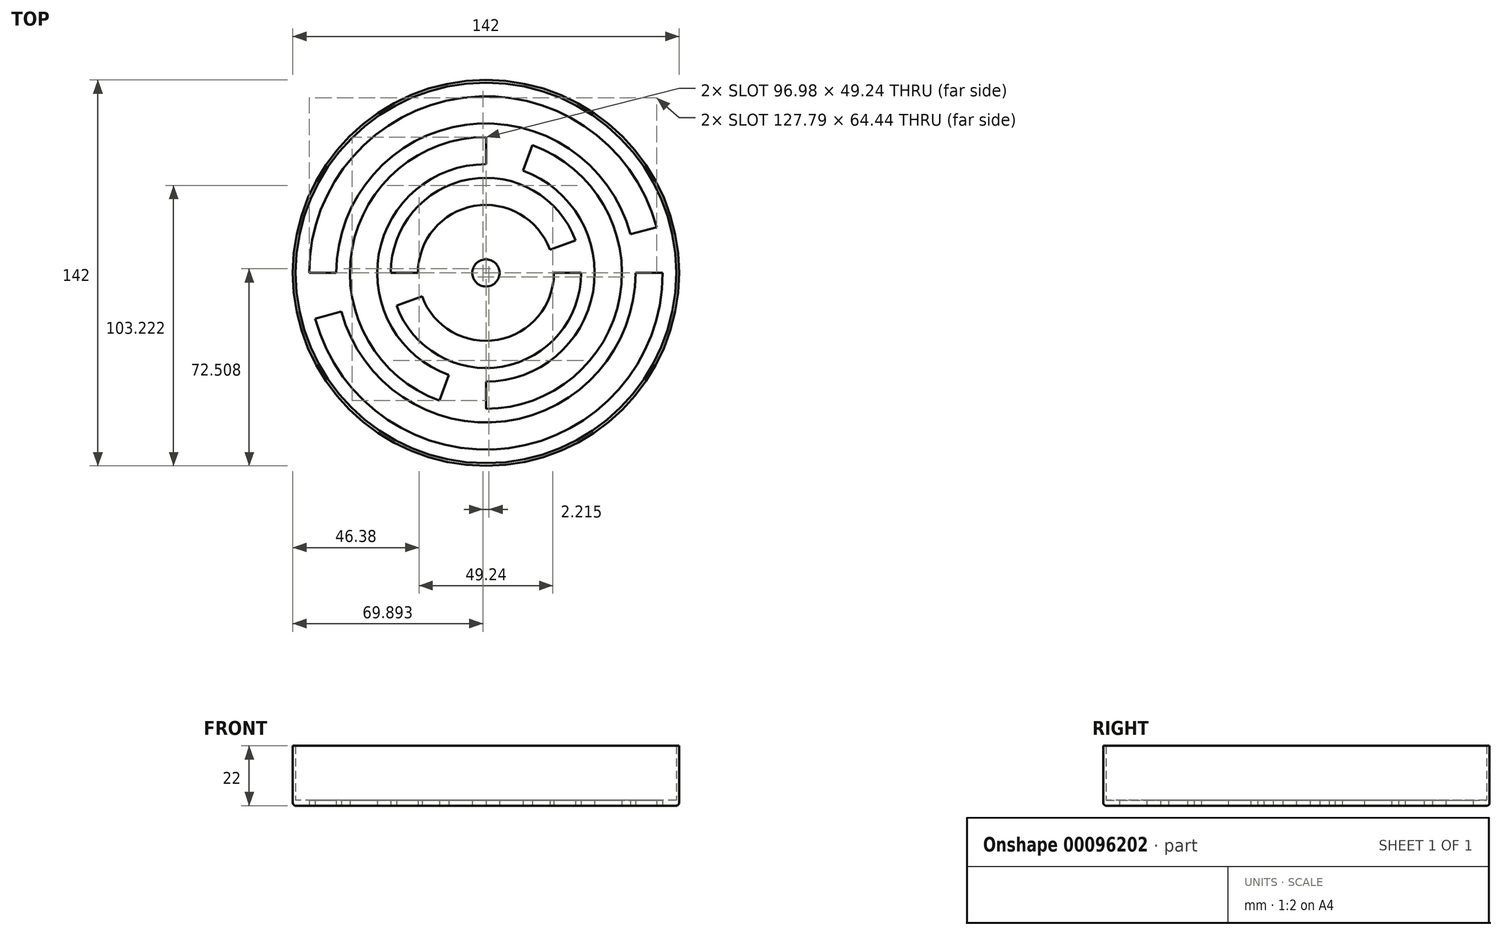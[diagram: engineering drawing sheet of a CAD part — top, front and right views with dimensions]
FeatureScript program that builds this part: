
annotation { "Feature Type Name" : "Feature", "Feature Type Description" : "" }
export const myFeature = defineFeature(function(context is Context, id is Id, definition is map)
    precondition{}
    {
        {
            assignVariable(context, id + "F0", {"name" : "wallthickness", "anyValue" : 2});
        }
        {
            assignVariable(context, id + "F1", {"name" : "height", "anyValue" : 20});
        }
        {
            var Q0;
            Q0=qCreatedBy(makeId("Top.planeOp"),FACE);
            var sketch = newSketch(context, id + "F2", { "sketchPlane" : qUnion([Q0])});
            skCircle(sketch, "E0", {"center": v(0, 0) * mm, "radius": 70 * mm});
            skCircle(sketch, "E1", {"center": v(0, 0) * mm, "radius": 71 * mm});
            skCircle(sketch, "E2", {"center": v(0, 0) * mm, "radius": 65 * mm});
            skCircle(sketch, "E3", {"center": v(0, 0) * mm, "radius": 55 * mm});
            skCircle(sketch, "E4", {"center": v(0, 0) * mm, "radius": 50 * mm});
            skCircle(sketch, "E5", {"center": v(0, 0) * mm, "radius": 40 * mm});
            skCircle(sketch, "E6", {"center": v(0, 0) * mm, "radius": 35 * mm});
            skCircle(sketch, "E7", {"center": v(0, 0) * mm, "radius": 25 * mm});
            skCircle(sketch, "E8", {"center": v(0, 0) * mm, "radius": 5 * mm});
            skLineSegment(sketch, "E9", {"start": v(-70, 0) * mm, "end": v(70, 0) * mm, "construction": true});
            skLineSegment(sketch, "E10", {"start": v(67.61, 18.12) * mm, "end": v(-67.61, -18.12) * mm, "construction": true});
            skLineSegment(sketch, "E11", {"start": v(23.94, 65.78) * mm, "end": v(-23.94, -65.78) * mm, "construction": true});
            skLineSegment(sketch, "E12", {"start": v(0, -50) * mm, "end": v(0, 50) * mm, "construction": true});
            skLineSegment(sketch, "E13", {"start": v(-65.78, -23.94) * mm, "end": v(65.78, 23.94) * mm, "construction": true});
            skLineSegment(sketch, "E14", {"start": v(-65, 0) * mm, "end": v(-55, 0) * mm});
            skLineSegment(sketch, "E15", {"start": v(-62.79, -16.82) * mm, "end": v(-53.13, -14.24) * mm});
            skLineSegment(sketch, "E16", {"start": v(55, 0) * mm, "end": v(65, 0) * mm});
            skLineSegment(sketch, "E17", {"start": v(62.79, 16.82) * mm, "end": v(53.13, 14.24) * mm});
            skLineSegment(sketch, "E18", {"start": v(35, 0) * mm, "end": v(25, 0) * mm});
            skLineSegment(sketch, "E19", {"start": v(32.89, 11.97) * mm, "end": v(23.5, 8.55) * mm});
            skLineSegment(sketch, "E20", {"start": v(-25, 0) * mm, "end": v(-35, 0) * mm});
            skLineSegment(sketch, "E21", {"start": v(-23.5, -8.55) * mm, "end": v(-32.89, -11.97) * mm});
            skLineSegment(sketch, "E22", {"start": v(-13.68, -37.59) * mm, "end": v(-17.1, -46.98) * mm});
            skLineSegment(sketch, "E23", {"start": v(0, -40) * mm, "end": v(0, -50) * mm});
            skLineSegment(sketch, "E24", {"start": v(0, 50) * mm, "end": v(0, 40) * mm});
            skLineSegment(sketch, "E25", {"start": v(17.1, 46.98) * mm, "end": v(13.68, 37.59) * mm});
            skSolve(sketch);
        }
        {
            var Q0;
            Q0=makeQuery(id+"F2.imprint","IMPRINT",FACE,{"disambiguationData":[TD([[makeQuery(id+"F2.imprint","IMPRINT",EDGE,{"derivedFrom":sQuery(id+"F2.wireOp",EDGE,"E0")}),-1.0]])]});
            extrude(context, id + "F3", {"entities" : qUnion([Q0]), "depth" : (getVariable(context, 'height') + getVariable(context, 'wallthickness')) * mm});
        }
        {
            var Q0;
            Q0=makeQuery(id+"F2.imprint","IMPRINT",FACE,{"disambiguationData":[TD([[makeQuery(id+"F2.imprint","IMPRINT",EDGE,{"derivedFrom":sQuery(id+"F2.wireOp",EDGE,"E8")}),-1.0]])]});
            var Q1;
            {var subQ0=sQuery(id+"F2.wireOp",EDGE,"E20");Q1=makeQuery(id+"F2.imprint","IMPRINT",FACE,{"disambiguationData":[TD([[makeQuery(id+"F2.imprint","IMPRINT",EDGE,{"derivedFrom":subQ0}),1.0]])]});}
            var Q2;
            {var subQ0=sQuery(id+"F2.wireOp",EDGE,"E18");Q2=makeQuery(id+"F2.imprint","IMPRINT",FACE,{"disambiguationData":[TD([[makeQuery(id+"F2.imprint","IMPRINT",EDGE,{"derivedFrom":subQ0}),-1.0]])]});}
            var Q3;
            {var subQ0=sQuery(id+"F2.wireOp",EDGE,"E5");var subQ4=makeQuery(id+"F2.imprint","INTERSECT",VERTEX,{"derivedFrom":[subQ0,sQuery(id+"F2.wireOp",EDGE,"E24")]});Q3=makeQuery(id+"F2.imprint","IMPRINT",FACE,{"disambiguationData":[TD([[makeQuery(id+"F2.imprint","IMPRINT",EDGE,{"disambiguationData":[TD([[subQ4,1.0]])],"derivedFrom":subQ0}),1.0]])]});}
            var Q4;
            {var subQ0=sQuery(id+"F2.wireOp",EDGE,"E22");Q4=makeQuery(id+"F2.imprint","IMPRINT",FACE,{"disambiguationData":[TD([[makeQuery(id+"F2.imprint","IMPRINT",EDGE,{"derivedFrom":subQ0}),1.0]])]});}
            var Q5;
            {var subQ0=sQuery(id+"F2.wireOp",EDGE,"E24");Q5=makeQuery(id+"F2.imprint","IMPRINT",FACE,{"disambiguationData":[TD([[makeQuery(id+"F2.imprint","IMPRINT",EDGE,{"derivedFrom":subQ0}),1.0]])]});}
            var Q6;
            {var subQ0=sQuery(id+"F2.wireOp",EDGE,"E3");var subQ2=makeQuery(id+"F2.imprint","INTERSECT",VERTEX,{"derivedFrom":[subQ0,sQuery(id+"F2.wireOp",EDGE,"E16")]});Q6=makeQuery(id+"F2.imprint","IMPRINT",FACE,{"disambiguationData":[TD([[makeQuery(id+"F2.imprint","IMPRINT",EDGE,{"disambiguationData":[TD([[subQ2,-1.0]])],"derivedFrom":subQ0}),1.0]])]});}
            var Q7;
            {var subQ0=sQuery(id+"F2.wireOp",EDGE,"E14");Q7=makeQuery(id+"F2.imprint","IMPRINT",FACE,{"disambiguationData":[TD([[makeQuery(id+"F2.imprint","IMPRINT",EDGE,{"derivedFrom":subQ0}),-1.0]])]});}
            var Q8;
            Q8=makeQuery(id+"F2.imprint","IMPRINT",FACE,{"disambiguationData":[TD([[makeQuery(id+"F2.imprint","IMPRINT",EDGE,{"derivedFrom":sQuery(id+"F2.wireOp",EDGE,"E0")}),1.0]])]});
            var Q9;
            {var subQ0=sQuery(id+"F2.wireOp",EDGE,"E16");Q9=makeQuery(id+"F2.imprint","IMPRINT",FACE,{"disambiguationData":[TD([[makeQuery(id+"F2.imprint","IMPRINT",EDGE,{"derivedFrom":subQ0}),1.0]])]});}
            extrude(context, id + "F4", {"entities" : qUnion([Q0, Q1, Q2, Q3, Q4, Q5, Q6, Q7, Q8, Q9]), "operationType" : NewBodyOperationType.ADD, "depth" : (getVariable(context, 'wallthickness')) * mm});
        }
        {
            var Q0;
            Q0=makeQuery(id+"F3.opExtrude","CAP_EDGE",EDGE,{"disambiguationData":[OSD([sQuery(id+"F2.wireOp",EDGE,"E1")])],"isStart":true});
            fillet(context, id + "F5", {"entities" : qUnion([Q0]), "radius" : 1 * mm, "tangentPropagation" : true, "allowEdgeOverflow" : false});
        }
    });
